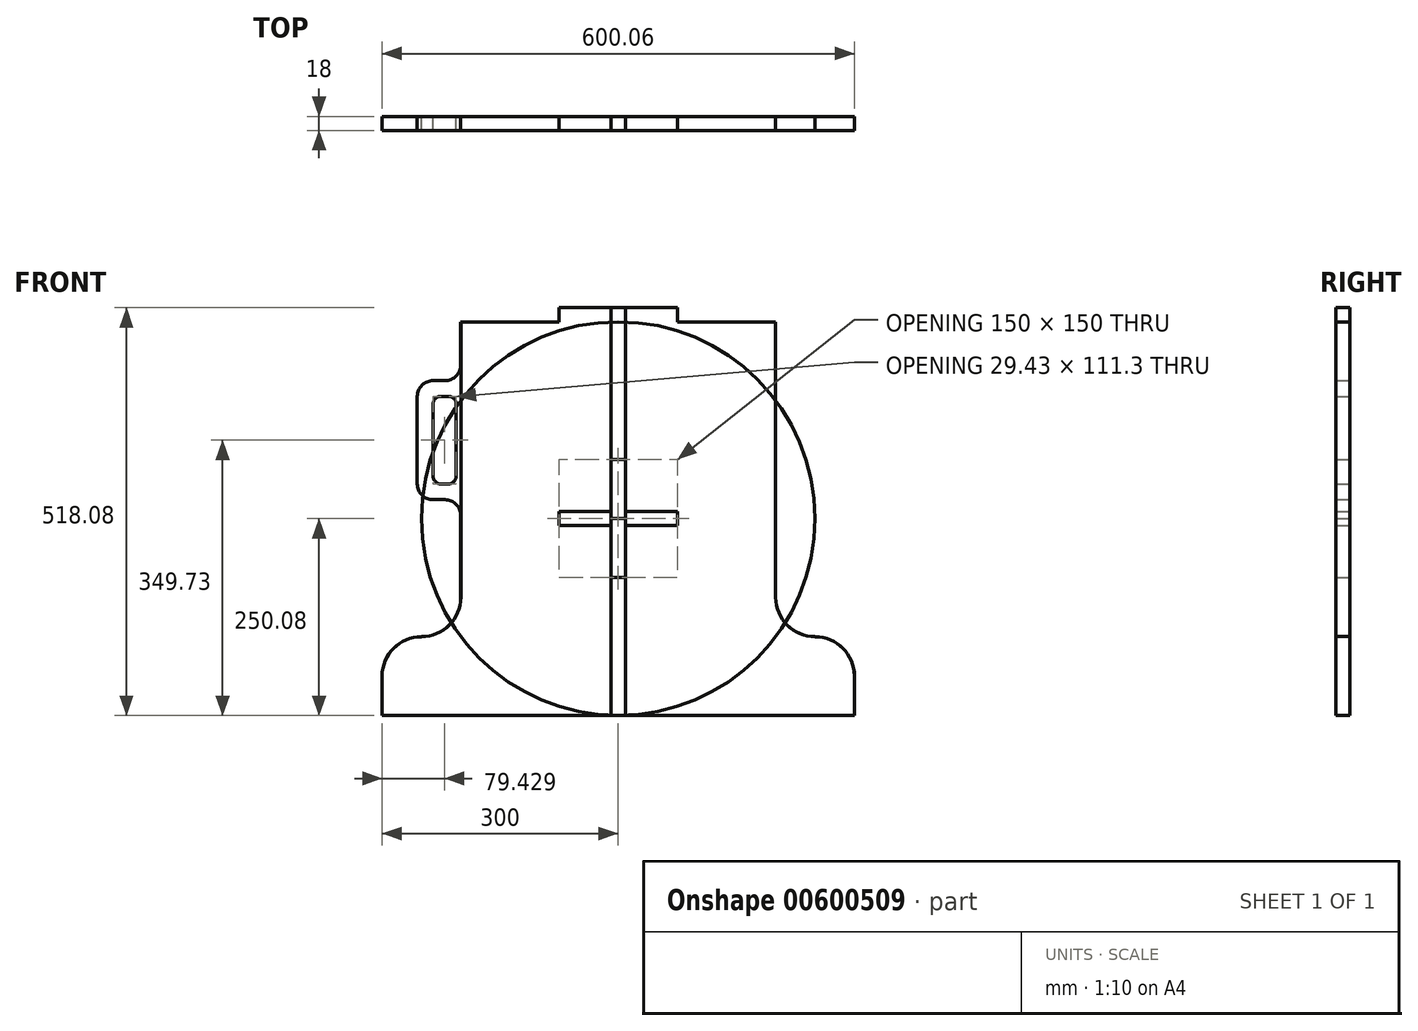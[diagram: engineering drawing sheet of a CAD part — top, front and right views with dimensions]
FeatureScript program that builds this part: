
annotation { "Feature Type Name" : "Feature", "Feature Type Description" : "" }
export const myFeature = defineFeature(function(context is Context, id is Id, definition is map)
    precondition{}
    {
        {
            var Q0;
            Q0=qCreatedBy(makeId("Front.planeOp"),FACE);
            var sketch = newSketch(context, id + "F0", { "sketchPlane" : qUnion([Q0])});
            skLineSegment(sketch, "E0.bottom", {"start": v(200, -250) * mm, "end": v(-200, -250) * mm});
            skLineSegment(sketch, "E0.top", {"start": v(200, 250) * mm, "end": v(75, 250) * mm});
            skLineSegment(sketch, "E0.left", {"start": v(200, -100) * mm, "end": v(200, 250) * mm});
            skLineSegment(sketch, "E0.right", {"start": v(-200, -100) * mm, "end": v(-200, 4) * mm});
            skPoint(sketch, "E0.middle", {"position": v(0, 0) * mm});
            skLineSegment(sketch, "E1.top", {"start": v(75, 268) * mm, "end": v(9, 268) * mm});
            skLineSegment(sketch, "E2.trimOffspring", {"start": v(-75, 250) * mm, "end": v(-200, 250) * mm});
            skLineSegment(sketch, "E3.trimOffspring", {"start": v(75, 250) * mm, "end": v(75, 268) * mm});
            skLineSegment(sketch, "E4.trimOffspring", {"start": v(-75, 250) * mm, "end": v(-75, 268) * mm});
            skLineSegment(sketch, "E5", {"start": v(200, -250) * mm, "end": v(300, -250) * mm});
            skLineSegment(sketch, "E6", {"start": v(300, -250) * mm, "end": v(300, -200) * mm});
            skLineSegment(sketch, "E7", {"start": v(250, -150) * mm, "end": v(250, -150) * mm});
            skPoint(sketch, "E8.newPointA", {"position": v(200, -150) * mm});
            skArc(sketch, "E8.filletArc", {"start": v(200, -100) * mm, "mid": v(214.64, -135.36) * mm, "end": v(250, -150) * mm});
            skPoint(sketch, "E9.visualSharp", {"position": v(300, -150) * mm});
            skArc(sketch, "E9.filletArc", {"start": v(300, -200) * mm, "mid": v(285.36, -164.64) * mm, "end": v(250, -150) * mm});
            skLineSegment(sketch, "E10", {"start": v(-200, -250) * mm, "end": v(-300, -250) * mm});
            skLineSegment(sketch, "E11", {"start": v(-300, -250) * mm, "end": v(-300, -200) * mm});
            skLineSegment(sketch, "E12", {"start": v(-250, -150) * mm, "end": v(-250, -150) * mm});
            skPoint(sketch, "E13.newPointA", {"position": v(-200, -250) * mm});
            skPoint(sketch, "E13.newPointB", {"position": v(-200, -150) * mm});
            skArc(sketch, "E13.filletArc", {"start": v(-250, -150) * mm, "mid": v(-214.64, -135.36) * mm, "end": v(-200, -100) * mm});
            skPoint(sketch, "E14.visualSharp", {"position": v(-300, -150) * mm});
            skArc(sketch, "E14.filletArc", {"start": v(-250, -150) * mm, "mid": v(-285.36, -164.64) * mm, "end": v(-300, -200) * mm});
            skLineSegment(sketch, "E15", {"start": v(-9, 0) * mm, "end": v(9, 0) * mm});
            skLineSegment(sketch, "E16.trimOffspring", {"start": v(-9, 268) * mm, "end": v(-75, 268) * mm});
            skLineSegment(sketch, "E17.trimOffspring", {"start": v(9, 0) * mm, "end": v(9, 268) * mm});
            skLineSegment(sketch, "E18.trimOffspring", {"start": v(-9, 0) * mm, "end": v(-9, 268) * mm});
            skLineSegment(sketch, "E19", {"start": v(-220, 175.3) * mm, "end": v(-235.28, 175.3) * mm});
            skLineSegment(sketch, "E20", {"start": v(-255.28, 155.3) * mm, "end": v(-255.28, 44) * mm});
            skLineSegment(sketch, "E21", {"start": v(-235.28, 24) * mm, "end": v(-220, 24) * mm});
            skLineSegment(sketch, "E22.trimOffspring", {"start": v(-200, 195.3) * mm, "end": v(-200, 250) * mm});
            skPoint(sketch, "E23.visualSharp", {"position": v(-200, 175.3) * mm});
            skArc(sketch, "E23.filletArc", {"start": v(-220, 175.3) * mm, "mid": v(-205.86, 181.16) * mm, "end": v(-200, 195.3) * mm});
            skPoint(sketch, "E24.visualSharp", {"position": v(-200, 24) * mm});
            skArc(sketch, "E24.filletArc", {"start": v(-200, 4) * mm, "mid": v(-205.86, 18.14) * mm, "end": v(-220, 24) * mm});
            skPoint(sketch, "E25.visualSharp", {"position": v(-255.28, 175.3) * mm});
            skArc(sketch, "E25.filletArc", {"start": v(-235.28, 175.3) * mm, "mid": v(-249.43, 169.44) * mm, "end": v(-255.28, 155.3) * mm});
            skPoint(sketch, "E26.visualSharp", {"position": v(-255.28, 24) * mm});
            skArc(sketch, "E26.filletArc", {"start": v(-255.28, 44) * mm, "mid": v(-249.43, 29.86) * mm, "end": v(-235.28, 24) * mm});
            skPoint(sketch, "E27.oppositeSnap0", {"position": v(-205.86, 18.14) * mm});
            skLineSegment(sketch, "E27.bottom", {"start": v(-225.28, 155.3) * mm, "end": v(-215.86, 155.3) * mm});
            skLineSegment(sketch, "E27.top", {"start": v(-225.28, 44) * mm, "end": v(-215.86, 44) * mm});
            skLineSegment(sketch, "E27.left", {"start": v(-235.28, 145.3) * mm, "end": v(-235.28, 54) * mm});
            skLineSegment(sketch, "E27.right", {"start": v(-205.86, 145.3) * mm, "end": v(-205.86, 54) * mm});
            skPoint(sketch, "E28.visualSharp", {"position": v(-205.86, 155.3) * mm});
            skArc(sketch, "E28.filletArc", {"start": v(-205.86, 145.3) * mm, "mid": v(-208.79, 152.37) * mm, "end": v(-215.86, 155.3) * mm});
            skPoint(sketch, "E29.visualSharp", {"position": v(-205.86, 44) * mm});
            skArc(sketch, "E29.filletArc", {"start": v(-215.86, 44) * mm, "mid": v(-208.79, 46.93) * mm, "end": v(-205.86, 54) * mm});
            skArc(sketch, "E30.filletArc", {"start": v(-235.28, 54) * mm, "mid": v(-232.36, 46.93) * mm, "end": v(-225.28, 44) * mm});
            skArc(sketch, "E31.filletArc", {"start": v(-225.28, 155.3) * mm, "mid": v(-232.36, 152.37) * mm, "end": v(-235.28, 145.3) * mm});
            skSolve(sketch);
        }
        {
            var Q0;
            Q0=qCreatedBy(makeId("Front.planeOp"),FACE);
            var sketch = newSketch(context, id + "F1", { "sketchPlane" : qUnion([Q0])});
            skLineSegment(sketch, "E32.bottom", {"start": v(200.06, -250.08) * mm, "end": v(9, -250.08) * mm});
            skLineSegment(sketch, "E32.top", {"start": v(200.06, 249.92) * mm, "end": v(75.06, 249.92) * mm});
            skLineSegment(sketch, "E32.left", {"start": v(200.06, -100.08) * mm, "end": v(200.06, 249.92) * mm});
            skLineSegment(sketch, "E32.right", {"start": v(-199.94, -100.08) * mm, "end": v(-199.94, 249.92) * mm});
            skPoint(sketch, "E32.middle", {"position": v(0.06, -0.08) * mm});
            skLineSegment(sketch, "E33.top", {"start": v(75.06, 267.92) * mm, "end": v(-74.94, 267.92) * mm});
            skLineSegment(sketch, "E34.trimOffspring", {"start": v(-74.94, 249.92) * mm, "end": v(-199.94, 249.92) * mm});
            skLineSegment(sketch, "E35.trimOffspring", {"start": v(75.06, 249.92) * mm, "end": v(75.06, 267.92) * mm});
            skLineSegment(sketch, "E36.trimOffspring", {"start": v(-74.94, 249.92) * mm, "end": v(-74.94, 267.92) * mm});
            skLineSegment(sketch, "E37", {"start": v(200.06, -250.08) * mm, "end": v(300.06, -250.08) * mm});
            skLineSegment(sketch, "E38", {"start": v(300.06, -250.08) * mm, "end": v(300.06, -200.08) * mm});
            skLineSegment(sketch, "E39", {"start": v(250.06, -150.08) * mm, "end": v(250.06, -150.08) * mm});
            skPoint(sketch, "E40.newPointA", {"position": v(200.06, -150.08) * mm});
            skArc(sketch, "E40.filletArc", {"start": v(200.06, -100.08) * mm, "mid": v(214.7, -135.43) * mm, "end": v(250.06, -150.08) * mm});
            skPoint(sketch, "E41.visualSharp", {"position": v(300.06, -150.08) * mm});
            skArc(sketch, "E41.filletArc", {"start": v(300.06, -200.08) * mm, "mid": v(285.41, -164.72) * mm, "end": v(250.06, -150.08) * mm});
            skLineSegment(sketch, "E42", {"start": v(-199.94, -250.08) * mm, "end": v(-299.94, -250.08) * mm});
            skLineSegment(sketch, "E43", {"start": v(-299.94, -250.08) * mm, "end": v(-299.94, -200.08) * mm});
            skLineSegment(sketch, "E44", {"start": v(-249.94, -150.08) * mm, "end": v(-249.94, -150.08) * mm});
            skPoint(sketch, "E45.newPointA", {"position": v(-199.94, -250.08) * mm});
            skPoint(sketch, "E45.newPointB", {"position": v(-199.94, -150.08) * mm});
            skArc(sketch, "E45.filletArc", {"start": v(-249.94, -150.08) * mm, "mid": v(-214.59, -135.43) * mm, "end": v(-199.94, -100.08) * mm});
            skPoint(sketch, "E46.visualSharp", {"position": v(-299.94, -150.08) * mm});
            skArc(sketch, "E46.filletArc", {"start": v(-249.94, -150.08) * mm, "mid": v(-285.3, -164.72) * mm, "end": v(-299.94, -200.08) * mm});
            skLineSegment(sketch, "E47.left", {"start": v(9, -250.08) * mm, "end": v(9, 0) * mm});
            skLineSegment(sketch, "E47.right", {"start": v(-9, -250.08) * mm, "end": v(-9, 0) * mm});
            skPoint(sketch, "E47.middle", {"position": v(0, 0) * mm});
            skLineSegment(sketch, "E48", {"start": v(-9, 0) * mm, "end": v(9, 0) * mm});
            skLineSegment(sketch, "E49.trimOffspring", {"start": v(-9, -250.08) * mm, "end": v(-199.94, -250.08) * mm});
            skSolve(sketch);
        }
        {
            var Q0;
            Q0 = qSketchRegion(id + "F0", true);
            extrude(context, id + "F2", {"entities" : qUnion([Q0]), "depth" : 18 * mm, "offsetDistance" : 25 * mm});
        }
        {
            var Q0;
            Q0 = qSketchRegion(id + "F1", true);
            extrude(context, id + "F3", {"entities" : qUnion([Q0]), "depth" : 18 * mm, "offsetDistance" : 25 * mm});
        }
        {
            var Q0;
            Q0=qCreatedBy(makeId("Front.planeOp"),FACE);
            var sketch = newSketch(context, id + "F4", { "sketchPlane" : qUnion([Q0])});
            skCircle(sketch, "E50", {"center": v(0, 0) * mm, "radius": 250 * mm});
            skLineSegment(sketch, "E51.bottom", {"start": v(75, -9) * mm, "end": v(9, -9) * mm});
            skLineSegment(sketch, "E51.top", {"start": v(75, 9) * mm, "end": v(9, 9) * mm});
            skLineSegment(sketch, "E51.left", {"start": v(75, -9) * mm, "end": v(75, 9) * mm});
            skLineSegment(sketch, "E51.right", {"start": v(-75, -9) * mm, "end": v(-75, 9) * mm});
            skLineSegment(sketch, "E52.bottom", {"start": v(9, -75) * mm, "end": v(-9, -75) * mm});
            skLineSegment(sketch, "E52.top", {"start": v(9, 75) * mm, "end": v(-9, 75) * mm});
            skLineSegment(sketch, "E52.left", {"start": v(9, -75) * mm, "end": v(9, -9) * mm});
            skLineSegment(sketch, "E52.right", {"start": v(-9, -75) * mm, "end": v(-9, -9) * mm});
            skLineSegment(sketch, "E53.trimOffspring", {"start": v(-9, 9) * mm, "end": v(-75, 9) * mm});
            skLineSegment(sketch, "E54.trimOffspring", {"start": v(-9, 9) * mm, "end": v(-9, 75) * mm});
            skLineSegment(sketch, "E55.trimOffspring", {"start": v(9, 9) * mm, "end": v(9, 75) * mm});
            skLineSegment(sketch, "E56.trimOffspring", {"start": v(-9, -9) * mm, "end": v(-75, -9) * mm});
            skSolve(sketch);
        }
        {
            var Q0;
            Q0=makeQuery(id+"F4.imprint","IMPRINT",FACE,{"disambiguationData":[TD([[makeQuery(id+"F4.imprint","IMPRINT",EDGE,{"derivedFrom":sQuery(id+"F4.wireOp",EDGE,"E50")}),1.0]])]});
            extrude(context, id + "F5", {"entities" : qUnion([Q0]), "depth" : 18 * mm, "offsetDistance" : 25 * mm});
        }
    });
